# Revit family: CT728CU GCU_TUS
name_source: partatom
category: Plumbing Fixtures
revit_build: Autodesk Revit 2018 (Build: 20170223_1515(x64)
units: mm (PartAtom-declared; Revit-internal decimal feet)

## family parameters
Always vertical = Yes
Cut with Voids When Loaded = No
OmniClass Number = 23.45.00.00
OmniClass Title = Sanitary, Laundry, and Cleaning Equipment
Part Type = Normal
Room Calculation Point = No
Round Connector Dimension = Use Diameter
Shared = No
Work Plane-Based = No

## types (1)
- CT728CU GCU_TUS
    CW Connection = Yes
    Description = Wall-mounted Toilet(Top Spud)
    Finish = White
    HW Connection = No
    Height = 342 mm  [stored 1.12205 ft]
    Length = 637 mm  [stored 2.0899 ft]
    Manufacturer = TOTO LTD.
    Material = Ceramic
    Model = CT728CUGX/CT728CUG/CT728CUX/CT728CU
    Seat Included = No
    URL = https://www.totousa.com
    Vent Connection = No
    Waste Connection = Yes
    Water Use = 1.0/1.28/1.6gpf
    Width = 350 mm  [stored 1.14829 ft]

note: [stored X ft] marks values corroborated as IEEE doubles in the binary element streams (Revit-internal decimal feet)

## geometry (parser evidence)
native form markers: Sweep x2
no freeform markers — native parametric forms only
